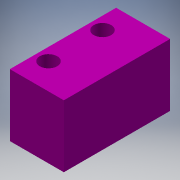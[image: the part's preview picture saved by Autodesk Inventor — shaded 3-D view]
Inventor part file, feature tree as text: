
AUTODESK INVENTOR PART (.ipt)
format: ipt  version: 2016 (Build 200138000, 138)  size: 91,136 bytes
history: native  units: mm
features: other x1, extrude x1, hole x1, sketch x1
ambient origin geometry x8: Origin, YZ Plane, XZ Plane, XY Plane, X Axis, Y Axis, Z Axis, Center Point
bodies: Solid1 (feature_tree)
feature tree (4):
  other  "Endstop.ipt"
  extrude  "Extrusion1"  Depth=7.5mm TaperAngle=0.0deg
  hole  "Hole1"  [1 undecoded]
  sketch  "Sketch1"  dims[d0=10.0mm d1=7.5mm d2=0.0mm d3=2.1mm d4=6.0mm d5=4.0mm d6=2.0mm d7=90.0deg d8=8.0mm d9=20.594885mm]
note: 1 required parameter value undecoded (feature->parameter linkage not recoverable at this tier; creation-order binding heuristic only, values carry confidence <= 0.55)
